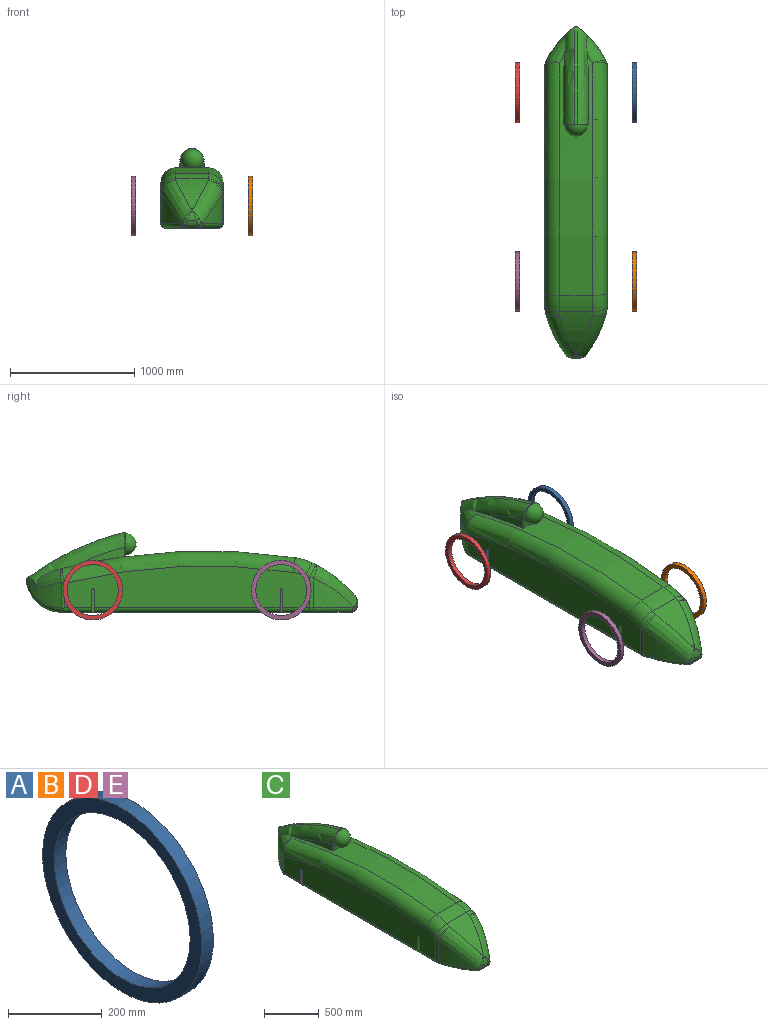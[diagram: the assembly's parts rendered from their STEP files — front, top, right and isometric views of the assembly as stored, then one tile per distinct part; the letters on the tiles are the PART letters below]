
ASSEMBLY  parts=5 mates=4
PART A: 4 faces, bbox 35x480x480 mm
  f0: cylinder r=205mm len=410mm, axis (-1,0,0), area 45081.9mm2, adj f2,f3
  f1: cylinder r=240mm len=480mm, axis (-1,0,0), area 52778.8mm2, adj f2,f3
  f2: plane 480x480mm, normal (1,0,0), area 48930.3mm2, adj f0,f1
  f3: plane 480x480mm, normal (-1,0,0), area 48930.3mm2, adj f0,f1
PART B: same geometry as A
PART C: 87 faces, bbox 520.9x2816.3x893 mm
  f0: plane 2310.7x420mm, normal (0,0,-1), area 931114.7mm2, adj f10,f66,f68,f69,f70,f80,f81,f82
  f1: cylinder r=997.58mm len=22.54mm, axis (-1,0,0), area 320.2mm2, adj f3,f5,f64,f75
  f2: cylinder r=1027.92mm len=329.56mm, axis (0,0,-1), area 49306.6mm2, adj f3,f20,f70,f71
  f3: bspline ~430.97x387.3mm, area 68048.1mm2, adj f1,f2,f9,f19,f63,f64,f72,f73
  f4: cylinder r=1027.92mm len=329.56mm, axis (0,0,-1), area 49306.6mm2, adj f5,f43,f79,f80
  f5: bspline ~402.88x374.05mm, area 68048.4mm2, adj f1,f4,f9,f42,f63,f64,f76,f77
  f6: plane 42.64x4.92mm, normal (0,-1,0), area 62.9mm2, adj f25,f48,f59,f62
  f7: plane 1972.62x334.51mm, normal (1,0,0), area 579237.8mm2, adj f16,f17,f18,f20,f22,f27,f28,f30
  f8: cylinder r=500mm len=260mm, axis (-1,0,0), area 36136.1mm2, adj f9,f11,f18,f41
  f9: cylinder r=997.58mm len=329.05mm, axis (-1,0,0), area 62618.3mm2, adj f3,f5,f8,f17,f40,f63
  f10: cylinder r=301.66mm len=410.71mm, axis (-1,0,0), area 78607mm2, adj f0,f84,f86
  f11: cylinder r=4818.85mm len=1936.61mm, axis (-1,0,0), area 391190.9mm2, adj f8,f12,f13,f15,f16,f24,f26,f36
  f12: plane 190x115.72mm, normal (0,-1,0), area 6283.9mm2, adj f11,f25,f26,f48,f49,f59
  f13: plane 397.98x149.39mm, normal (1,0,0), area 17346.3mm2, adj f11,f24,f26
  f14: cylinder r=798.12mm len=281.3mm, axis (0,0,-1), area 49042.8mm2, adj f15,f22,f23,f24,f61,f85,f86
  f15: bspline ~276.58x255.68mm, area 28319.2mm2, adj f11,f14,f21,f24
  f16: torus R=4698.85mm, axis (1,0,0), area 353885.5mm2, adj f7,f11,f18,f21,f23
  f17: torus R=877.58mm, axis (1,0,0), area 6765.5mm2, adj f7,f9,f18,f19
  f18: torus R=380mm, axis (1,0,0), area 23913.3mm2, adj f7,f8,f16,f17
  f19: sphere r=120mm, area 3285.3mm2, adj f3,f17,f20
  f20: cylinder r=120mm len=237.86mm, axis (0,0,-1), area 7717.1mm2, adj f2,f7,f19,f69
  f21: bspline ~119.31x113.18mm, area 1569.3mm2, adj f15,f16,f23
  f22: cylinder r=50mm len=203.73mm, axis (0,0,-1), area 4595.4mm2, adj f7,f14,f23,f68,f85
  f23: bspline ~28.81x24.97mm, area 233.9mm2, adj f14,f16,f21,f22
  f24: torus R=2073.72mm, axis (-1,0,0), area 111219.6mm2, adj f11,f13,f14,f15,f25,f61
  f25: bspline ~135.56x91.83mm, area 1318.2mm2, adj f6,f12,f24,f26,f60,f62
  f26: cylinder r=5mm len=77.36mm, axis (0,0,1), area 604.9mm2, adj f11,f12,f13,f25
  f27: plane 177.08x25mm, normal (0,1,0), area 4171mm2, adj f7,f29,f30,f68
  f28: plane 177.08x25mm, normal (0,-1,0), area 4171mm2, adj f7,f29,f30,f68
  f29: plane 187.08x20mm, normal (1,0,0), area 3698.7mm2, adj f27,f28,f30,f68
  f30: cylinder r=10mm len=25mm, axis (1,0,0), area 785.4mm2, adj f7,f27,f28,f29
  f31: plane 177.08x25mm, normal (0,-1,0), area 4171mm2, adj f7,f33,f34,f68
  f32: plane 177.08x25mm, normal (0,1,0), area 4171mm2, adj f7,f33,f34,f68
  f33: plane 187.08x20mm, normal (1,0,0), area 3698.7mm2, adj f31,f32,f34,f68
  f34: cylinder r=10mm len=25mm, axis (1,0,0), area 785.4mm2, adj f7,f31,f32,f33
  f35: plane 1972.62x334.51mm, normal (-1,0,0), area 579237.8mm2, adj f39,f40,f41,f43,f45,f50,f51,f53
  f36: plane 397.98x149.39mm, normal (-1,0,0), area 17346.3mm2, adj f11,f47,f49
  f37: cylinder r=798.12mm len=281.3mm, axis (0,0,-1), area 49041.7mm2, adj f38,f45,f46,f47,f61,f83,f84
  f38: bspline ~276.58x255.68mm, area 28319.2mm2, adj f11,f37,f44,f47
  f39: torus R=4698.85mm, axis (-1,0,0), area 353885.5mm2, adj f11,f35,f41,f44,f46
  f40: torus R=877.58mm, axis (-1,0,0), area 6765.5mm2, adj f9,f35,f41,f42
  f41: torus R=380mm, axis (-1,0,0), area 23913.3mm2, adj f8,f35,f39,f40
  f42: sphere r=120mm, area 3285.3mm2, adj f5,f40,f43
  f43: cylinder r=120mm len=237.86mm, axis (0,0,-1), area 7717.1mm2, adj f4,f35,f42,f81
  f44: bspline ~119.31x113.18mm, area 1569mm2, adj f38,f39,f46
  f45: cylinder r=50mm len=203.73mm, axis (0,0,-1), area 4595.4mm2, adj f35,f37,f46,f82,f83
  f46: bspline ~28.81x24.97mm, area 233.9mm2, adj f37,f39,f44,f45
  f47: torus R=2073.72mm, axis (1,0,0), area 111216.4mm2, adj f11,f36,f37,f38,f48,f61
  f48: bspline ~135.56x91.83mm, area 1318.2mm2, adj f6,f12,f47,f49,f58,f62
  f49: cylinder r=5mm len=77.36mm, axis (0,0,1), area 604.9mm2, adj f11,f12,f36,f48
  f50: plane 177.08x25mm, normal (0,1,0), area 4171mm2, adj f35,f52,f53,f82
  f51: plane 177.08x25mm, normal (0,-1,0), area 4171mm2, adj f35,f52,f53,f82
  f52: plane 187.08x20mm, normal (-1,0,0), area 3698.7mm2, adj f50,f51,f53,f82
  f53: cylinder r=10mm len=25mm, axis (-1,0,0), area 785.4mm2, adj f35,f50,f51,f52
  f54: plane 177.08x25mm, normal (0,-1,0), area 4171mm2, adj f35,f56,f57,f82
  f55: plane 177.08x25mm, normal (0,1,0), area 4171mm2, adj f35,f56,f57,f82
  f56: plane 187.08x20mm, normal (-1,0,0), area 3698.7mm2, adj f54,f55,f57,f82
  f57: cylinder r=10mm len=25mm, axis (-1,0,0), area 785.4mm2, adj f35,f54,f55,f56
  f58: plane 71.78x67.35mm, normal (0,1,0), area 257.9mm2, adj f48,f59
  f59: sphere r=90mm, area 50893.8mm2, adj f6,f12,f58,f60
  f60: plane 71.78x67.35mm, normal (0,1,0), area 257.9mm2, adj f25,f59
  f61: torus R=2140.81mm, axis (-1,0,0), area 25430.3mm2, adj f14,f24,f37,f47,f62,f84,f86
  f62: bspline ~37.73x10.08mm, area 254.7mm2, adj f6,f25,f48,f61
  f63: plane 30.96x0.18mm, normal (0,0.37,-0.93), area 3.5mm2, adj f3,f5,f9,f64
  f64: cylinder r=133.28mm len=30.9mm, axis (1,0,0), area 16mm2, adj f1,f3,f5,f63
  f65: cylinder r=133.28mm len=73.03mm, axis (1,0,0), area 3412.7mm2, adj f67,f74,f75,f76
  f66: cylinder r=69mm len=125.34mm, axis (1,0,0), area 6411.7mm2, adj f0,f67,f71,f72,f78,f79
  f67: cylinder r=69mm len=94.46mm, axis (1,0,0), area 3822.8mm2, adj f65,f66,f72,f73,f77,f78
  f68: cylinder r=40mm len=1983.9mm, axis (0,-1,0), area 122461.3mm2, adj f0,f7,f22,f27,f28,f29,f31,f32
  f69: torus R=80mm, axis (0,0,1), area 1791.6mm2, adj f0,f20,f68,f70
  f70: torus R=987.92mm, axis (0,0,1), area 21865.3mm2, adj f0,f2,f69,f71
  f71: bspline ~49.75x44.38mm, area 1345.6mm2, adj f2,f66,f70,f72
  f72: bspline ~55.53x46.46mm, area 1320.5mm2, adj f3,f66,f67,f71,f73
  f73: bspline ~60.51x43.8mm, area 1310.2mm2, adj f3,f67,f72,f74
  f74: bspline ~86.62x66.99mm, area 1313.4mm2, adj f3,f65,f73,f75
  f75: cylinder r=40mm len=3.52mm, axis (-1,0,0), area 10.2mm2, adj f1,f65,f74,f76
  f76: bspline ~86.62x66.99mm, area 1313.4mm2, adj f5,f65,f75,f77
  f77: bspline ~60.51x43.8mm, area 1310.2mm2, adj f5,f67,f76,f78
  f78: bspline ~55.53x46.46mm, area 1320.5mm2, adj f5,f66,f67,f77,f79
  f79: bspline ~53.38x46.06mm, area 1345.6mm2, adj f4,f66,f78,f80
  f80: torus R=987.92mm, axis (0,0,1), area 21865.3mm2, adj f0,f4,f79,f81
  f81: torus R=80mm, axis (0,0,1), area 1791.6mm2, adj f0,f43,f80,f82
  f82: cylinder r=40mm len=1983.9mm, axis (0,-1,0), area 122461.3mm2, adj f0,f35,f45,f50,f51,f52,f54,f55
  f83: torus R=758.12mm, axis (0,0,1), area 943.2mm2, adj f0,f37,f45,f82,f84
  f84: bspline ~310.3x282.07mm, area 20891.1mm2, adj f10,f37,f61,f83,f86
  f85: torus R=758.12mm, axis (0,0,1), area 943.2mm2, adj f0,f14,f22,f68,f86
  f86: bspline ~310.3x282.07mm, area 20891.1mm2, adj f10,f14,f61,f84,f85
PART D: same geometry as A
PART E: same geometry as A
PLACE A t=(323.45,861.79,11.49)mm
PLACE B t=(323.45,-656.21,11.49)mm
PLACE C t=(-129.05,601.79,-168.51)mm fixed
PLACE D t=(-616.55,861.79,11.49)mm
PLACE E t=(-616.55,-656.21,11.49)mm
MATE fastened C.f34 <-> B.f0  axis (1,0,0) through (120.95,-656.21,11.49)mm
MATE fastened E.f0 <-> C.f34  axis (1,0,0) through (-581.55,-656.21,11.49)mm
MATE fastened A.f0 <-> C.f30  axis (-1,0,0) through (323.45,861.79,11.49)mm
MATE fastened D.f0 <-> C.f30  axis (1,0,0) through (-581.55,861.79,11.49)mm
